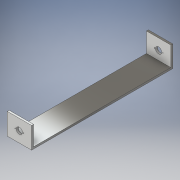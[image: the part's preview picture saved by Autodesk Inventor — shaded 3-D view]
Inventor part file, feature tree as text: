
AUTODESK INVENTOR PART (.ipt)
format: ipt  version: 2019 (Build 230136000, 136)  size: 142,848 bytes
history: native  units: in
note: dims shown in document units (in); Inventor stores cm internally (conversion verified against a paired STEP export)
features: extrude x3, sketch x3, projected_geometry x2
ambient origin geometry x8: Origin, YZ Plane, XZ Plane, XY Plane, X Axis, Y Axis, Z Axis, Center Point
bodies: Solid1 (feature_tree)
feature tree (8):
  extrude  "Extrusion1"  Depth=5.7087in
  extrude  "Extrusion2"  Depth=0.0787in
  extrude  "Extrusion4"  Depth=0.7874in TaperAngle=0.0deg
  sketch  "Sketch1"  dims[d0=0.9843in d1=5.7087in]
  sketch  "Sketch2"  dims[d2=0.0787in d3=0.0in d4=0.0787in]
  projected_geometry  "Projected Loop1"
  sketch  "Sketch3"  dims[d5=0.0787in d6=0.7874in d7=0.0in d8=0.4921in d9=0.4331in d10=0.25in d15=0.0312in d16=0.0312in d17=0.3241in d19=0.3241in d20=0.4331in d21=0.4331in d22=0.7874in d23=0.0in]
  projected_geometry  "Projected Loop2"
